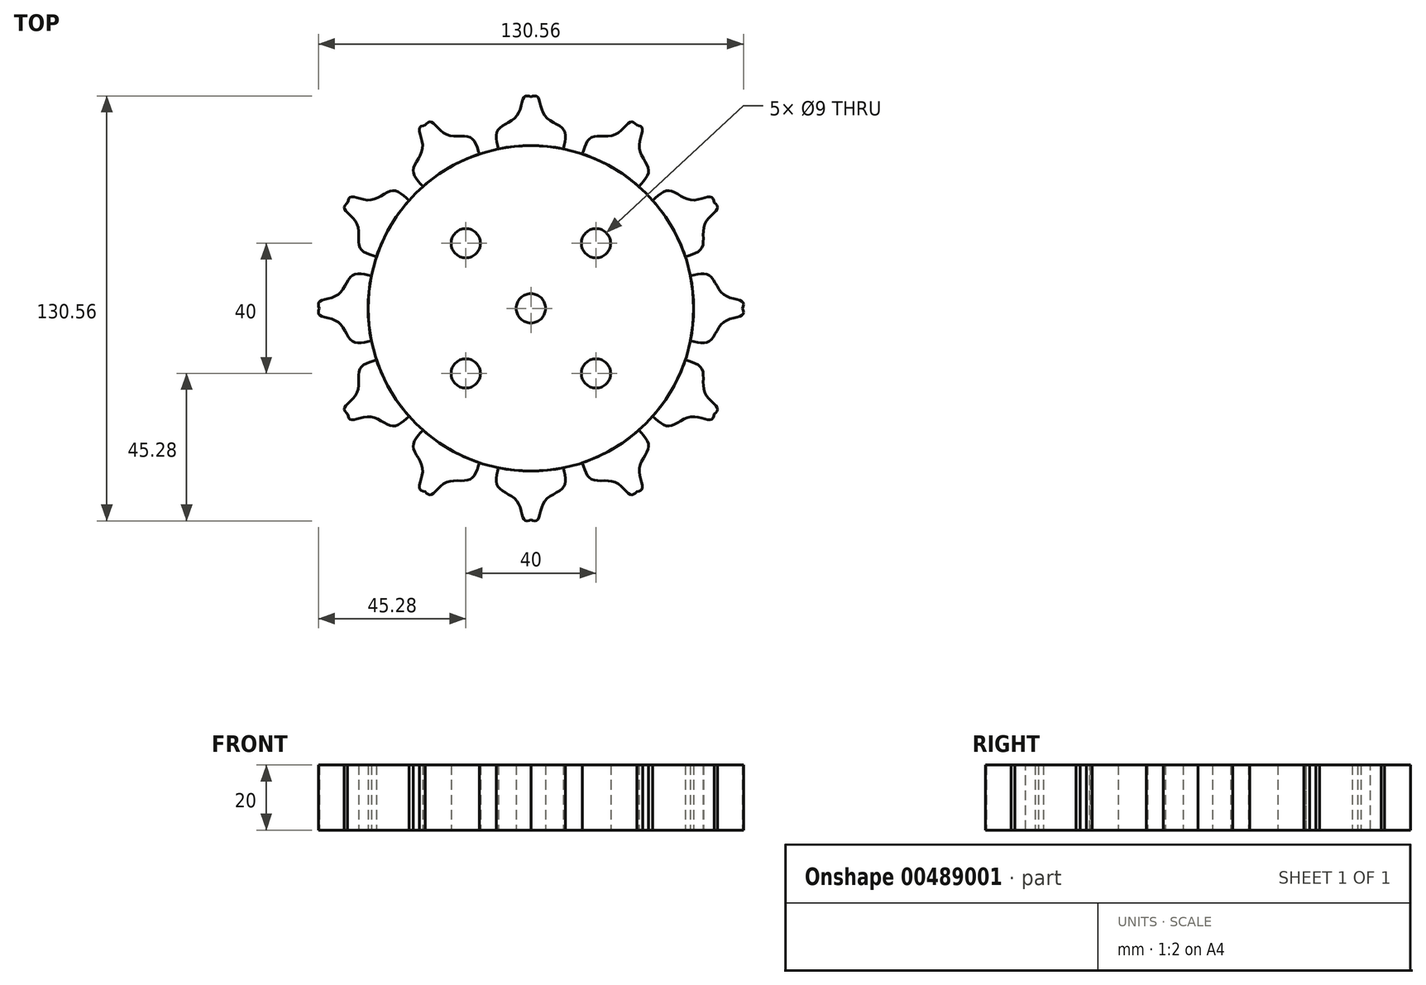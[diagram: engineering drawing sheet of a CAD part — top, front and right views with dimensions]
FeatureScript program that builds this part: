
annotation { "Feature Type Name" : "Feature", "Feature Type Description" : "" }
export const myFeature = defineFeature(function(context is Context, id is Id, definition is map)
    precondition{}
    {
        {
            var Q0;
            Q0=qCreatedBy(makeId("Top.planeOp"),FACE);
            var sketch = newSketch(context, id + "F0", { "sketchPlane" : qUnion([Q0])});
            skCircle(sketch, "E0", {"center": v(0, 0) * mm, "radius": 50 * mm});
            skLineSegment(sketch, "E1", {"start": v(-0.1, 0) * mm, "end": v(0, 55) * mm, "construction": true});
            skLineSegment(sketch, "E2", {"start": v(0, 55) * mm, "end": v(0, 65) * mm, "construction": true});
            skLineSegment(sketch, "E3", {"start": v(0, 55) * mm, "end": v(10, 54.98) * mm, "construction": true});
            skLineSegment(sketch, "E4", {"start": v(0, 55) * mm, "end": v(4.24, 59.25) * mm, "construction": true});
            skLineSegment(sketch, "E5", {"start": v(0, 65) * mm, "end": v(2, 65) * mm, "construction": true});
            skFitSpline(sketch, "E6", {"points": [v(0, 65) * mm, v(2, 65) * mm, v(4.24, 59.25) * mm, v(10, 54.98) * mm, v(10, 48.99) * mm], "startDerivative": vector(14.54, 4.6) * mm, "endDerivative": vector(-6.04, -25.64) * mm});
            skFitSpline(sketch, "E7.MirrorCS", {"points": [v(0, 65) * mm, v(-2, 65) * mm, v(-4.24, 59.25) * mm, v(-10, 54.98) * mm, v(-10, 48.99) * mm], "startDerivative": vector(-14.54, 4.6) * mm, "endDerivative": vector(6.04, -25.64) * mm});
            skLineSegment(sketch, "E8", {"start": v(0, 0) * mm, "end": v(20, 0) * mm, "construction": true});
            skLineSegment(sketch, "E9", {"start": v(20, 0) * mm, "end": v(20, 20) * mm, "construction": true});
            skCircle(sketch, "E10", {"center": v(20, 20) * mm, "radius": 4.5 * mm});
            skCircle(sketch, "E11.1.0", {"center": v(-20, 20) * mm, "radius": 4.5 * mm});
            skCircle(sketch, "E11.2.0", {"center": v(-20, -20) * mm, "radius": 4.5 * mm});
            skCircle(sketch, "E11.3.0", {"center": v(20, -20) * mm, "radius": 4.5 * mm});
            skCircle(sketch, "E12", {"center": v(0, 0) * mm, "radius": 4.5 * mm});
            skSolve(sketch);
        }
        {
            var Q0;
            {var subQ0=sQuery(id+"F0.wireOp",EDGE,"E6");Q0=makeQuery(id+"F0.imprint","IMPRINT",FACE,{"disambiguationData":[TD([[makeQuery(id+"F0.imprint","IMPRINT",EDGE,{"derivedFrom":subQ0}),-1.0]])]});}
            extrude(context, id + "F1", {"entities" : qUnion([Q0]), "depth" : 20 * mm});
        }
        {
            var Q0;
            Q0=makeQuery(id+"F1.opExtrude","SWEPT_BODY",BODY,{"disambiguationData":[OSD([sQuery(id+"F0.wireOp",EDGE,"E0"),sQuery(id+"F0.wireOp",EDGE,"E6"),sQuery(id+"F0.wireOp",EDGE,"E7.MirrorCS")])]});
            var Q1;
            Q1=sQuery(id+"F0.wireOp",EDGE,"E0");
            circularPattern(context, id + "F2", {"entities" : qUnion([Q0]), "axis" : qUnion([Q1]), "angle" : 360 * degree, "instanceCount" : 12, "equalSpace" : true});
        }
        {
            var Q0;
            Q0=makeQuery(id+"F0.imprint","IMPRINT",FACE,{"disambiguationData":[TD([[makeQuery(id+"F0.imprint","IMPRINT",EDGE,{"derivedFrom":sQuery(id+"F0.wireOp",EDGE,"E10")}),-1.0]])]});
            extrude(context, id + "F3", {"entities" : qUnion([Q0]), "depth" : 20 * mm});
        }
    });
